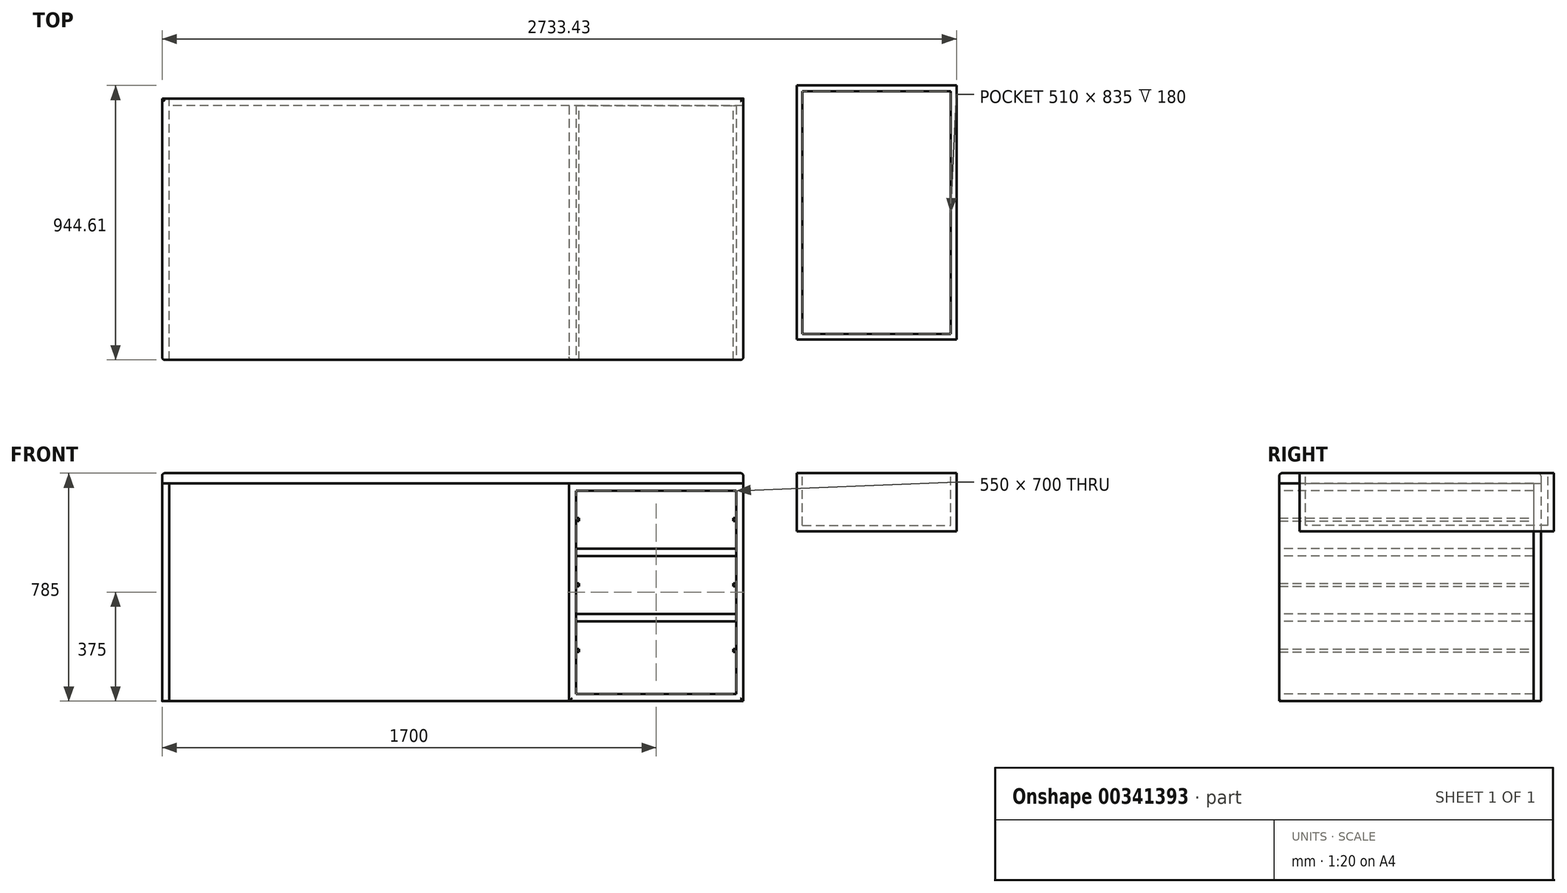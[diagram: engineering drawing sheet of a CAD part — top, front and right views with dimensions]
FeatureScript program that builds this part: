
annotation { "Feature Type Name" : "Feature", "Feature Type Description" : "" }
export const myFeature = defineFeature(function(context is Context, id is Id, definition is map)
    precondition{}
    {
        {
            var Q0;
            Q0=qCreatedBy(makeId("Top.planeOp"),FACE);
            var sketch = newSketch(context, id + "F0", { "sketchPlane" : qUnion([Q0])});
            skLineSegment(sketch, "E0.bottom", {"start": v(0, 0) * mm, "end": v(-2000, 0) * mm});
            skLineSegment(sketch, "E0.top", {"start": v(0, 900) * mm, "end": v(-2000, 900) * mm});
            skLineSegment(sketch, "E0.left", {"start": v(0, 0) * mm, "end": v(0, 900) * mm});
            skLineSegment(sketch, "E0.right", {"start": v(-2000, 0) * mm, "end": v(-2000, 900) * mm});
            skSolve(sketch);
        }
        {
            var Q0;
            Q0=makeQuery(id+"F0.imprint","IMPRINT",FACE,{"disambiguationData":[TD([[makeQuery(id+"F0.imprint","IMPRINT",EDGE,{"derivedFrom":sQuery(id+"F0.wireOp",EDGE,"E0.bottom")}),-1.0]])]});
            extrude(context, id + "F1", {"entities" : qUnion([Q0]), "depth" : 35 * mm});
        }
        {
            var Q0;
            Q0=makeQuery(id+"F1.opExtrude","CAP_EDGE",EDGE,{"disambiguationData":[OSD([sQuery(id+"F0.wireOp",EDGE,"E0.right")])],"isStart":false});
            var Q1;
            Q1=makeQuery(id+"F1.opExtrude","CAP_EDGE",EDGE,{"disambiguationData":[OSD([sQuery(id+"F0.wireOp",EDGE,"E0.top")])],"isStart":false});
            var Q2;
            Q2=makeQuery(id+"F1.opExtrude","CAP_EDGE",EDGE,{"disambiguationData":[OSD([sQuery(id+"F0.wireOp",EDGE,"E0.left")])],"isStart":false});
            var Q3;
            Q3=makeQuery(id+"F1.opExtrude","CAP_EDGE",EDGE,{"disambiguationData":[OSD([sQuery(id+"F0.wireOp",EDGE,"E0.bottom")])],"isStart":false});
            fillet(context, id + "F2", {"entities" : qUnion([Q0, Q1, Q2, Q3]), "radius" : 10 * mm, "tangentPropagation" : true, "allowEdgeOverflow" : false});
        }
        {
            var Q0;
            Q0=qCreatedBy(makeId("Front.planeOp"),FACE);
            var sketch = newSketch(context, id + "F3", { "sketchPlane" : qUnion([Q0])});
            skLineSegment(sketch, "E1.bottom", {"start": v(0, 0) * mm, "end": v(-600, 0) * mm});
            skLineSegment(sketch, "E1.top", {"start": v(0, -750) * mm, "end": v(-600, -750) * mm});
            skLineSegment(sketch, "E1.left", {"start": v(0, 0) * mm, "end": v(0, -750) * mm});
            skLineSegment(sketch, "E1.right", {"start": v(-600, 0) * mm, "end": v(-600, -750) * mm});
            skLineSegment(sketch, "E2.bottom", {"start": v(-575, -25) * mm, "end": v(-25, -25) * mm});
            skLineSegment(sketch, "E2.top", {"start": v(-575, -725) * mm, "end": v(-25, -725) * mm});
            skLineSegment(sketch, "E2.left", {"start": v(-575, -25) * mm, "end": v(-575, -725) * mm});
            skLineSegment(sketch, "E2.right", {"start": v(-25, -25) * mm, "end": v(-25, -725) * mm});
            skPoint(sketch, "E3.start.orphan", {"position": v(-600, -375) * mm});
            skSolve(sketch);
        }
        {
            var Q0;
            Q0=makeQuery(id+"F3.imprint","IMPRINT",FACE,{"disambiguationData":[TD([[makeQuery(id+"F3.imprint","IMPRINT",EDGE,{"derivedFrom":sQuery(id+"F3.wireOp",EDGE,"E1.bottom")}),1.0]])]});
            extrude(context, id + "F4", {"entities" : qUnion([Q0]), "oppositeDirection" : true, "depth" : 875 * mm});
        }
        {
            var Q0;
            Q0=makeQuery(id+"F4.opExtrude","CAP_EDGE",EDGE,{"disambiguationData":[OSD([sQuery(id+"F3.wireOp",EDGE,"E1.right")])],"isStart":true});
            var Q1;
            Q1=makeQuery(id+"F4.opExtrude","CAP_EDGE",EDGE,{"disambiguationData":[OSD([sQuery(id+"F3.wireOp",EDGE,"E1.top")])],"isStart":true});
            var Q2;
            Q2=makeQuery(id+"F4.opExtrude","CAP_EDGE",EDGE,{"disambiguationData":[OSD([sQuery(id+"F3.wireOp",EDGE,"E1.left")])],"isStart":true});
            fillet(context, id + "F5", {"entities" : qUnion([Q0, Q1, Q2]), "radius" : 10 * mm, "tangentPropagation" : true, "allowEdgeOverflow" : false});
        }
        {
            var Q0;
            Q0=makeQuery(id+"F1.opExtrude","SWEPT_FACE",FACE,{"disambiguationData":[OSD([sQuery(id+"F0.wireOp",EDGE,"E0.right")])]});
            var sketch = newSketch(context, id + "F6", { "sketchPlane" : qUnion([Q0])});
            skLineSegment(sketch, "E4.bottom", {"start": v(-900, 0) * mm, "end": v(0, 0) * mm});
            skLineSegment(sketch, "E4.top", {"start": v(-900, -750) * mm, "end": v(0, -750) * mm});
            skLineSegment(sketch, "E4.left", {"start": v(-900, 0) * mm, "end": v(-900, -750) * mm});
            skLineSegment(sketch, "E4.right", {"start": v(0, 0) * mm, "end": v(0, -750) * mm});
            skSolve(sketch);
        }
        {
            var Q0;
            Q0=makeQuery(id+"F6.imprint","IMPRINT",FACE,{"disambiguationData":[TD([[makeQuery(id+"F6.imprint","IMPRINT",EDGE,{"derivedFrom":sQuery(id+"F6.wireOp",EDGE,"E4.bottom")}),1.0]])]});
            extrude(context, id + "F7", {"entities" : qUnion([Q0]), "oppositeDirection" : true, "depth" : 25 * mm});
        }
        {
            var Q0;
            Q0=makeQuery(id+"F1.opExtrude","SWEPT_FACE",FACE,{"disambiguationData":[OSD([sQuery(id+"F0.wireOp",EDGE,"E0.top")])]});
            var sketch = newSketch(context, id + "F8", { "sketchPlane" : qUnion([Q0])});
            skLineSegment(sketch, "E5.bottom", {"start": v(1975, 0) * mm, "end": v(0, 0) * mm});
            skLineSegment(sketch, "E5.top", {"start": v(1975, -750) * mm, "end": v(0, -750) * mm});
            skLineSegment(sketch, "E5.left", {"start": v(1975, 0) * mm, "end": v(1975, -750) * mm});
            skLineSegment(sketch, "E5.right", {"start": v(0, 0) * mm, "end": v(0, -750) * mm});
            skSolve(sketch);
        }
        {
            var Q0;
            Q0=makeQuery(id+"F8.imprint","IMPRINT",FACE,{"disambiguationData":[TD([[makeQuery(id+"F8.imprint","IMPRINT",EDGE,{"derivedFrom":sQuery(id+"F8.wireOp",EDGE,"E5.bottom")}),-1.0]])]});
            extrude(context, id + "F9", {"entities" : qUnion([Q0]), "oppositeDirection" : true, "depth" : 25 * mm});
        }
        {
            var Q0;
            Q0=makeQuery(id+"F1.opExtrude","SWEPT_EDGE",EDGE,{"disambiguationData":[OSD([sQuery(id+"F0.wireOp",EDGE,"E0.bottom"),sQuery(id+"F0.wireOp",EDGE,"E0.right")])]});
            var Q1;
            Q1=makeQuery(id+"F7.opExtrude","CAP_EDGE",EDGE,{"disambiguationData":[OSD([sQuery(id+"F6.wireOp",EDGE,"E4.right")])],"isStart":true});
            fillet(context, id + "F10", {"entities" : qUnion([Q0, Q1]), "radius" : 10 * mm, "tangentPropagation" : true, "allowEdgeOverflow" : false});
        }
        {
            var Q0;
            Q0=makeQuery(id+"F1.opExtrude","SWEPT_EDGE",EDGE,{"disambiguationData":[OSD([sQuery(id+"F0.wireOp",EDGE,"E0.bottom"),sQuery(id+"F0.wireOp",EDGE,"E0.left")])]});
            fillet(context, id + "F11", {"entities" : qUnion([Q0]), "radius" : 10 * mm, "tangentPropagation" : true, "allowEdgeOverflow" : false});
        }
        {
            var Q0;
            Q0=makeQuery(id+"F4.opExtrude","CAP_FACE",FACE,{"disambiguationData":[OSD([sQuery(id+"F3.wireOp",EDGE,"E1.bottom"),sQuery(id+"F3.wireOp",EDGE,"E1.top"),sQuery(id+"F3.wireOp",EDGE,"E1.left"),sQuery(id+"F3.wireOp",EDGE,"E1.right"),sQuery(id+"F3.wireOp",EDGE,"E2.bottom"),sQuery(id+"F3.wireOp",EDGE,"E2.top"),sQuery(id+"F3.wireOp",EDGE,"E2.left"),sQuery(id+"F3.wireOp",EDGE,"E2.right")])],"isStart":true});
            var sketch = newSketch(context, id + "F12", { "sketchPlane" : qUnion([Q0])});
            skLineSegment(sketch, "E6.bottom", {"start": v(-575, -225) * mm, "end": v(-25, -225) * mm});
            skLineSegment(sketch, "E6.top", {"start": v(-575, -250) * mm, "end": v(-25, -250) * mm});
            skLineSegment(sketch, "E6.left", {"start": v(-575, -225) * mm, "end": v(-575, -250) * mm});
            skLineSegment(sketch, "E6.right", {"start": v(-25, -225) * mm, "end": v(-25, -250) * mm});
            skSolve(sketch);
        }
        {
            var Q0;
            Q0=makeQuery(id+"F12.imprint","IMPRINT",FACE,{"disambiguationData":[TD([[makeQuery(id+"F12.imprint","IMPRINT",EDGE,{"derivedFrom":sQuery(id+"F12.wireOp",EDGE,"E6.bottom")}),-1.0]])]});
            extrude(context, id + "F13", {"entities" : qUnion([Q0]), "oppositeDirection" : true, "depth" : 875 * mm});
        }
        {
            var Q0;
            Q0=makeQuery(id+"F4.opExtrude","CAP_FACE",FACE,{"disambiguationData":[OSD([sQuery(id+"F3.wireOp",EDGE,"E1.bottom"),sQuery(id+"F3.wireOp",EDGE,"E1.top"),sQuery(id+"F3.wireOp",EDGE,"E1.left"),sQuery(id+"F3.wireOp",EDGE,"E1.right"),sQuery(id+"F3.wireOp",EDGE,"E2.bottom"),sQuery(id+"F3.wireOp",EDGE,"E2.top"),sQuery(id+"F3.wireOp",EDGE,"E2.left"),sQuery(id+"F3.wireOp",EDGE,"E2.right")])],"isStart":true});
            var sketch = newSketch(context, id + "F14", { "sketchPlane" : qUnion([Q0])});
            skLineSegment(sketch, "E7.bottom", {"start": v(-575, -450) * mm, "end": v(-25, -450) * mm});
            skLineSegment(sketch, "E7.top", {"start": v(-575, -475) * mm, "end": v(-25, -475) * mm});
            skLineSegment(sketch, "E7.left", {"start": v(-575, -450) * mm, "end": v(-575, -475) * mm});
            skLineSegment(sketch, "E7.right", {"start": v(-25, -450) * mm, "end": v(-25, -475) * mm});
            skSolve(sketch);
        }
        {
            var Q0;
            Q0=makeQuery(id+"F14.imprint","IMPRINT",FACE,{"disambiguationData":[TD([[makeQuery(id+"F14.imprint","IMPRINT",EDGE,{"derivedFrom":sQuery(id+"F14.wireOp",EDGE,"E7.bottom")}),-1.0]])]});
            extrude(context, id + "F15", {"entities" : qUnion([Q0]), "oppositeDirection" : true, "depth" : 875 * mm});
        }
        {
            var Q0;
            Q0=makeQuery(id+"F4.opExtrude","SWEPT_FACE",FACE,{"disambiguationData":[OSD([sQuery(id+"F3.wireOp",EDGE,"E2.left")])]});
            var sketch = newSketch(context, id + "F16", { "sketchPlane" : qUnion([Q0])});
            skLineSegment(sketch, "E8.bottom", {"start": v(0, -345) * mm, "end": v(875, -345) * mm});
            skLineSegment(sketch, "E8.top", {"start": v(0, -355) * mm, "end": v(875, -355) * mm});
            skLineSegment(sketch, "E8.left", {"start": v(0, -345) * mm, "end": v(0, -355) * mm});
            skLineSegment(sketch, "E8.right", {"start": v(875, -345) * mm, "end": v(875, -355) * mm});
            skLineSegment(sketch, "E9.bottom", {"start": v(0, -120) * mm, "end": v(875, -120) * mm});
            skLineSegment(sketch, "E9.top", {"start": v(0, -130) * mm, "end": v(875, -130) * mm});
            skLineSegment(sketch, "E9.left", {"start": v(0, -120) * mm, "end": v(0, -130) * mm});
            skLineSegment(sketch, "E9.right", {"start": v(875, -120) * mm, "end": v(875, -130) * mm});
            skLineSegment(sketch, "E10.bottom", {"start": v(0, -570) * mm, "end": v(875, -570) * mm});
            skLineSegment(sketch, "E10.top", {"start": v(0, -580) * mm, "end": v(875, -580) * mm});
            skLineSegment(sketch, "E10.left", {"start": v(0, -570) * mm, "end": v(0, -580) * mm});
            skLineSegment(sketch, "E10.right", {"start": v(875, -570) * mm, "end": v(875, -580) * mm});
            skSolve(sketch);
        }
        {
            var Q0;
            Q0=makeQuery(id+"F16.imprint","IMPRINT",FACE,{"disambiguationData":[TD([[makeQuery(id+"F16.imprint","IMPRINT",EDGE,{"derivedFrom":sQuery(id+"F16.wireOp",EDGE,"E9.bottom")}),-1.0]])]});
            var Q1;
            Q1=makeQuery(id+"F16.imprint","IMPRINT",FACE,{"disambiguationData":[TD([[makeQuery(id+"F16.imprint","IMPRINT",EDGE,{"derivedFrom":sQuery(id+"F16.wireOp",EDGE,"E8.bottom")}),-1.0]])]});
            var Q2;
            Q2=makeQuery(id+"F16.imprint","IMPRINT",FACE,{"disambiguationData":[TD([[makeQuery(id+"F16.imprint","IMPRINT",EDGE,{"derivedFrom":sQuery(id+"F16.wireOp",EDGE,"E10.bottom")}),-1.0]])]});
            extrude(context, id + "F17", {"entities" : qUnion([Q0, Q1, Q2]), "depth" : 10 * mm});
        }
        {
            var Q0;
            Q0=makeQuery(id+"F4.opExtrude","SWEPT_FACE",FACE,{"disambiguationData":[OSD([sQuery(id+"F3.wireOp",EDGE,"E2.right")])]});
            var sketch = newSketch(context, id + "F18", { "sketchPlane" : qUnion([Q0])});
            skLineSegment(sketch, "E11.bottom", {"start": v(0, -120) * mm, "end": v(-875, -120) * mm});
            skLineSegment(sketch, "E11.top", {"start": v(0, -130) * mm, "end": v(-875, -130) * mm});
            skLineSegment(sketch, "E11.left", {"start": v(0, -120) * mm, "end": v(0, -130) * mm});
            skLineSegment(sketch, "E11.right", {"start": v(-875, -120) * mm, "end": v(-875, -130) * mm});
            skLineSegment(sketch, "E12.bottom", {"start": v(0, -355) * mm, "end": v(-875, -355) * mm});
            skLineSegment(sketch, "E12.top", {"start": v(0, -345) * mm, "end": v(-875, -345) * mm});
            skLineSegment(sketch, "E12.left", {"start": v(0, -355) * mm, "end": v(0, -345) * mm});
            skLineSegment(sketch, "E12.right", {"start": v(-875, -355) * mm, "end": v(-875, -345) * mm});
            skLineSegment(sketch, "E13.bottom", {"start": v(0, -580) * mm, "end": v(-875, -580) * mm});
            skLineSegment(sketch, "E13.top", {"start": v(0, -570) * mm, "end": v(-875, -570) * mm});
            skLineSegment(sketch, "E13.left", {"start": v(0, -580) * mm, "end": v(0, -570) * mm});
            skLineSegment(sketch, "E13.right", {"start": v(-875, -580) * mm, "end": v(-875, -570) * mm});
            skSolve(sketch);
        }
        {
            var Q0;
            Q0=makeQuery(id+"F18.imprint","IMPRINT",FACE,{"disambiguationData":[TD([[makeQuery(id+"F18.imprint","IMPRINT",EDGE,{"derivedFrom":sQuery(id+"F18.wireOp",EDGE,"E11.bottom")}),1.0]])]});
            var Q1;
            Q1=makeQuery(id+"F18.imprint","IMPRINT",FACE,{"disambiguationData":[TD([[makeQuery(id+"F18.imprint","IMPRINT",EDGE,{"derivedFrom":sQuery(id+"F18.wireOp",EDGE,"E12.bottom")}),-1.0]])]});
            var Q2;
            Q2=makeQuery(id+"F18.imprint","IMPRINT",FACE,{"disambiguationData":[TD([[makeQuery(id+"F18.imprint","IMPRINT",EDGE,{"derivedFrom":sQuery(id+"F18.wireOp",EDGE,"E13.bottom")}),-1.0]])]});
            extrude(context, id + "F19", {"entities" : qUnion([Q0, Q1, Q2]), "depth" : 10 * mm});
        }
        {
            var Q0;
            Q0=makeQuery(id+"F1.opExtrude","CAP_FACE",FACE,{"disambiguationData":[OSD([sQuery(id+"F0.wireOp",EDGE,"E0.bottom"),sQuery(id+"F0.wireOp",EDGE,"E0.top"),sQuery(id+"F0.wireOp",EDGE,"E0.left"),sQuery(id+"F0.wireOp",EDGE,"E0.right")])],"isStart":false});
            var sketch = newSketch(context, id + "F20", { "sketchPlane" : qUnion([Q0])});
            skLineSegment(sketch, "E14.bottom", {"start": v(183.43, 944.6) * mm, "end": v(733.43, 944.6) * mm});
            skLineSegment(sketch, "E14.top", {"start": v(183.43, 69.6) * mm, "end": v(733.43, 69.6) * mm});
            skLineSegment(sketch, "E14.left", {"start": v(183.43, 944.6) * mm, "end": v(183.43, 69.6) * mm});
            skLineSegment(sketch, "E14.right", {"start": v(733.43, 944.6) * mm, "end": v(733.43, 69.6) * mm});
            skLineSegment(sketch, "E15", {"start": v(1015.6, 1078.9) * mm, "end": v(1086.7, -290.92) * mm});
            skLineSegment(sketch, "E16.MirrorCS", {"start": v(183.43, 1819.6) * mm, "end": v(733.43, 1819.6) * mm});
            skLineSegment(sketch, "E17.MirrorCS", {"start": v(733.43, 944.6) * mm, "end": v(733.43, 1819.6) * mm});
            skLineSegment(sketch, "E18.MirrorCS", {"start": v(183.43, 944.6) * mm, "end": v(183.43, 1819.6) * mm});
            skSolve(sketch);
        }
        {
            var Q0;
            Q0=makeQuery(id+"F20.imprint","IMPRINT",FACE,{"disambiguationData":[TD([[makeQuery(id+"F20.imprint","IMPRINT",EDGE,{"derivedFrom":sQuery(id+"F20.wireOp",EDGE,"E14.bottom")}),-1.0]])]});
            extrude(context, id + "F21", {"entities" : qUnion([Q0]), "oppositeDirection" : true, "depth" : 200 * mm});
        }
        {
            var Q0;
            Q0=makeQuery(id+"F21.opExtrude","CAP_FACE",FACE,{"disambiguationData":[OSD([sQuery(id+"F20.wireOp",EDGE,"E14.bottom"),sQuery(id+"F20.wireOp",EDGE,"E14.top"),sQuery(id+"F20.wireOp",EDGE,"E14.left"),sQuery(id+"F20.wireOp",EDGE,"E14.right")])],"isStart":true});
            shell(context, id + "F22", {"entities" : qUnion([Q0]), "thickness" : 20 * mm});
        }
    });
